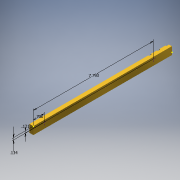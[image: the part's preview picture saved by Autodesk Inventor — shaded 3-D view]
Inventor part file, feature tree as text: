
AUTODESK INVENTOR PART (.ipt)
format: ipt  version: 2017 (Build 210142000, 142)  size: 179,712 bytes
history: native  units: in
note: dims shown in document units (in); Inventor stores cm internally (conversion verified against a paired STEP export)
features: sketch x3, hole x3, pattern_linear x3, extrude x2
ambient origin geometry x8: Origin, YZ Plane, XZ Plane, XY Plane, X Axis, Y Axis, Z Axis, Center Point
bodies: Solid1 (feature_tree)
feature tree (11):
  extrude  "Extrusion1"  Depth=0.5in
  sketch  "Sketch3"  dims[d6=9.0in d7=0.0in d8=0.1344in]
  hole  "Hole1"  [1 undecoded]
  pattern_linear  "Rectangular Pattern1"  Count1=7 Spacing1=1.0in
  sketch  "Sketch6"  dims[d9=0.7in d10=0.067in d11=0.75in d12=0.375in d13=0.25in d14=0.5635in d15=1.0in d16=0.8108in d17=2.7559in d19=1.0in d20=0.75in d23=0.8108in d24=0.5635in d25=0.25in d26=0.375in d27=0.25in d28=0.067in d45=7.793in d46=0.121in d61=0.067in d62=0.75in d63=0.375in d64=0.25in d65=0.5635in d66=0.25in d67=0.8108in d68=2.3in d69=0.15in d70=0.7874in d72=1.0in d73=1.9685in d75=1.5in d76=0.125in d77=0.125in d78=1.207in d85=1.0in d86=0.0in d93=0.16in d94=0.06in d95=0.06in d96=0.16in d97=0.06in]
  hole  "Hole5"  [1 undecoded]
  pattern_linear  "Rectangular Pattern5"  Spacing1=7.793in  [1 undecoded]
  pattern_linear  "Rectangular Pattern6"  Spacing1=0.121in  [1 undecoded]
  extrude  "Extrusion3"  Depth=0.06in
  sketch  "Sketch2"  dims[d3=0.25in d5=0.5in]
  hole  "Hole2"  [1 undecoded]
note: 5 required parameter values undecoded (feature->parameter linkage not recoverable at this tier; creation-order binding heuristic only, values carry confidence <= 0.55)
